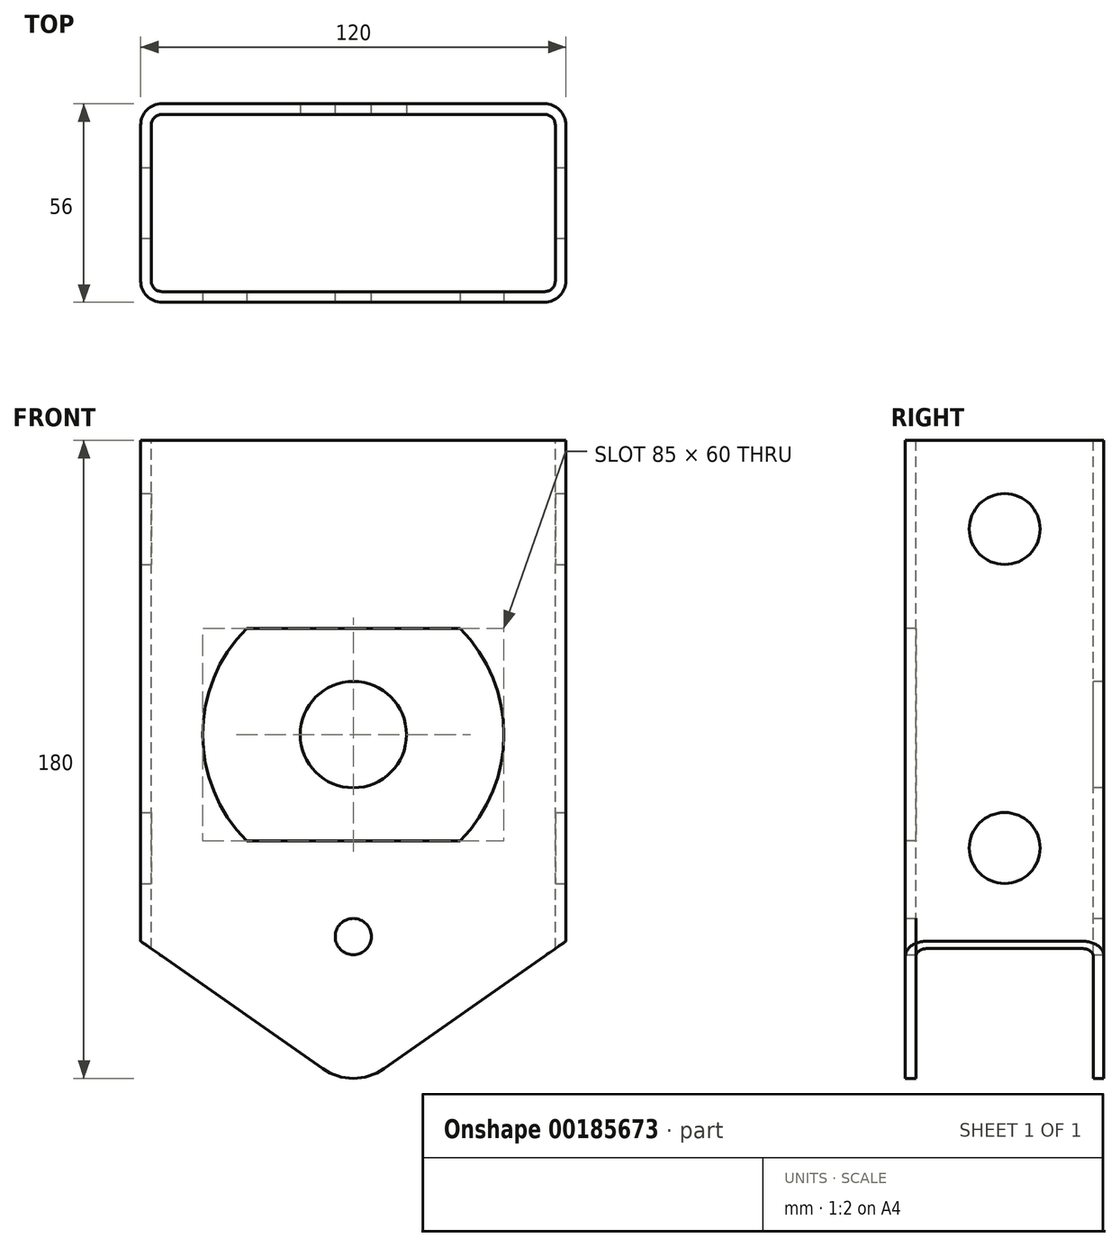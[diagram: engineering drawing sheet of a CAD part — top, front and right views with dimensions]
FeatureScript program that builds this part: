
annotation { "Feature Type Name" : "Feature", "Feature Type Description" : "" }
export const myFeature = defineFeature(function(context is Context, id is Id, definition is map)
    precondition{}
    {
        {
            var Q0;
            Q0=qCreatedBy(makeId("Front.planeOp"),FACE);
            var sketch = newSketch(context, id + "F0", { "sketchPlane" : qUnion([Q0])});
            skLineSegment(sketch, "E0.bottom", {"start": v(-60, 100) * mm, "end": v(60, 100) * mm});
            skLineSegment(sketch, "E0.left", {"start": v(-60, 100) * mm, "end": v(-60, -41.3) * mm});
            skLineSegment(sketch, "E0.right", {"start": v(60, 100) * mm, "end": v(60, -41.3) * mm});
            skArc(sketch, "E1", {"start": v(-8.6, -77.29) * mm, "mid": v(0, -80) * mm, "end": v(8.6, -77.29) * mm});
            skPoint(sketch, "E1.centerSnap0", {"position": v(0, -65) * mm});
            skLineSegment(sketch, "E2", {"start": v(60, -41.3) * mm, "end": v(8.6, -77.29) * mm});
            skLineSegment(sketch, "E3", {"start": v(-8.6, -77.29) * mm, "end": v(-60, -41.3) * mm});
            skPoint(sketch, "E4.orphan", {"position": v(0, -83.31) * mm});
            skCircle(sketch, "E5", {"center": v(0, -40) * mm, "radius": 5.1 * mm});
            skSolve(sketch);
        }
        {
            var Q0;
            Q0=qSketchRegion(id+"F0",true);
            extrude(context, id + "F1", {"entities" : qUnion([Q0]), "depth" : 56 * mm});
        }
        {
            var Q0;
            Q0=makeQuery(id+"F1.opExtrude","SWEPT_FACE",FACE,{"disambiguationData":[OSD([sQuery(id+"F0.wireOp",EDGE,"E0.bottom")])]});
            var sketch = newSketch(context, id + "F2", { "sketchPlane" : qUnion([Q0])});
            skLineSegment(sketch, "E6.bottom", {"start": v(-54, -3) * mm, "end": v(54, -3) * mm});
            skLineSegment(sketch, "E6.top", {"start": v(-54, -53) * mm, "end": v(54, -53) * mm});
            skLineSegment(sketch, "E6.left", {"start": v(-57, -6) * mm, "end": v(-57, -50) * mm});
            skLineSegment(sketch, "E6.right", {"start": v(57, -6) * mm, "end": v(57, -50) * mm});
            skPoint(sketch, "E7.visualSharp", {"position": v(57, -3) * mm});
            skArc(sketch, "E7.filletArc", {"start": v(57, -6) * mm, "mid": v(56.12, -3.88) * mm, "end": v(54, -3) * mm});
            skPoint(sketch, "E8.visualSharp", {"position": v(57, -53) * mm});
            skArc(sketch, "E8.filletArc", {"start": v(54, -53) * mm, "mid": v(56.12, -52.12) * mm, "end": v(57, -50) * mm});
            skPoint(sketch, "E9.visualSharp", {"position": v(-57, -3) * mm});
            skArc(sketch, "E9.filletArc", {"start": v(-54, -3) * mm, "mid": v(-56.12, -3.88) * mm, "end": v(-57, -6) * mm});
            skPoint(sketch, "E10.visualSharp", {"position": v(-57, -53) * mm});
            skArc(sketch, "E10.filletArc", {"start": v(-57, -50) * mm, "mid": v(-56.12, -52.12) * mm, "end": v(-54, -53) * mm});
            skSolve(sketch);
        }
        {
            var Q0;
            Q0=qSketchRegion(id+"F2",true);
            extrude(context, id + "F3", {"entities" : qUnion([Q0]), "operationType" : NewBodyOperationType.REMOVE, "endBound" : BoundingType.UP_TO_NEXT, "oppositeDirection" : true, "depth" : 25 * mm});
        }
        {
            var Q0;
            Q0=makeQuery(id+"F1.opExtrude","CAP_FACE",FACE,{"disambiguationData":[OSD([sQuery(id+"F0.wireOp",EDGE,"E0.bottom"),sQuery(id+"F0.wireOp",EDGE,"E0.left"),sQuery(id+"F0.wireOp",EDGE,"E0.right"),sQuery(id+"F0.wireOp",EDGE,"E1"),sQuery(id+"F0.wireOp",EDGE,"E2"),sQuery(id+"F0.wireOp",EDGE,"E3"),sQuery(id+"F0.wireOp",EDGE,"E5")])],"isStart":false});
            var sketch = newSketch(context, id + "F4", { "sketchPlane" : qUnion([Q0])});
            skArc(sketch, "E11", {"start": v(-30.1, 47) * mm, "mid": v(-42.5, 17) * mm, "end": v(-30.1, -13) * mm});
            skLineSegment(sketch, "E12", {"start": v(-30.1, 47) * mm, "end": v(30.1, 47) * mm});
            skLineSegment(sketch, "E13", {"start": v(30.1, -13) * mm, "end": v(-30.1, -13) * mm});
            skArc(sketch, "E14.trimOffspring", {"start": v(30.1, -13) * mm, "mid": v(42.5, 17) * mm, "end": v(30.1, 47) * mm});
            skSolve(sketch);
        }
        {
            var Q0;
            Q0=qSketchRegion(id+"F4",true);
            extrude(context, id + "F5", {"entities" : qUnion([Q0]), "operationType" : NewBodyOperationType.REMOVE, "endBound" : BoundingType.UP_TO_NEXT, "oppositeDirection" : true, "depth" : 25 * mm});
        }
        {
            var Q0;
            Q0=makeQuery(id+"F3.boolean.opBoolean","COPY",FACE,{"derivedFrom":makeQuery(id+"F3.opExtrude","SWEPT_FACE",FACE,{"disambiguationData":[OSD([sQuery(id+"F2.wireOp",EDGE,"E6.bottom")])]})});
            var sketch = newSketch(context, id + "F6", { "sketchPlane" : qUnion([Q0])});
            skCircle(sketch, "E15", {"center": v(0, 17) * mm, "radius": 15 * mm});
            skSolve(sketch);
        }
        {
            var Q0;
            Q0=qSketchRegion(id+"F6",true);
            extrude(context, id + "F7", {"entities" : qUnion([Q0]), "operationType" : NewBodyOperationType.REMOVE, "oppositeDirection" : true, "depth" : 25 * mm});
        }
        {
            var Q0;
            Q0=makeQuery(id+"F1.opExtrude","SWEPT_FACE",FACE,{"disambiguationData":[OSD([sQuery(id+"F0.wireOp",EDGE,"E0.right")])]});
            var sketch = newSketch(context, id + "F8", { "sketchPlane" : qUnion([Q0])});
            skCircle(sketch, "E16", {"center": v(-28, 75) * mm, "radius": 10 * mm});
            skCircle(sketch, "E17", {"center": v(-28, -15) * mm, "radius": 10 * mm});
            skSolve(sketch);
        }
        {
            var Q0;
            Q0=qSketchRegion(id+"F8",true);
            extrude(context, id + "F9", {"entities" : qUnion([Q0]), "operationType" : NewBodyOperationType.REMOVE, "endBound" : BoundingType.THROUGH_ALL, "oppositeDirection" : true, "depth" : 25 * mm});
        }
        {
            var Q0;
            Q0=makeQuery(id+"F1.opExtrude","CAP_EDGE",EDGE,{"disambiguationData":[OSD([sQuery(id+"F0.wireOp",EDGE,"E0.left")])],"isStart":false});
            var Q1;
            Q1=makeQuery(id+"F1.opExtrude","CAP_EDGE",EDGE,{"disambiguationData":[OSD([sQuery(id+"F0.wireOp",EDGE,"E0.right")])],"isStart":false});
            var Q2;
            Q2=makeQuery(id+"F1.opExtrude","CAP_EDGE",EDGE,{"disambiguationData":[OSD([sQuery(id+"F0.wireOp",EDGE,"E0.left")])],"isStart":true});
            var Q3;
            Q3=makeQuery(id+"F1.opExtrude","CAP_EDGE",EDGE,{"disambiguationData":[OSD([sQuery(id+"F0.wireOp",EDGE,"E0.right")])],"isStart":true});
            fillet(context, id + "F10", {"entities" : qUnion([Q0, Q1, Q2, Q3]), "radius" : 6 * mm, "tangentPropagation" : true, "allowEdgeOverflow" : false});
        }
    });
